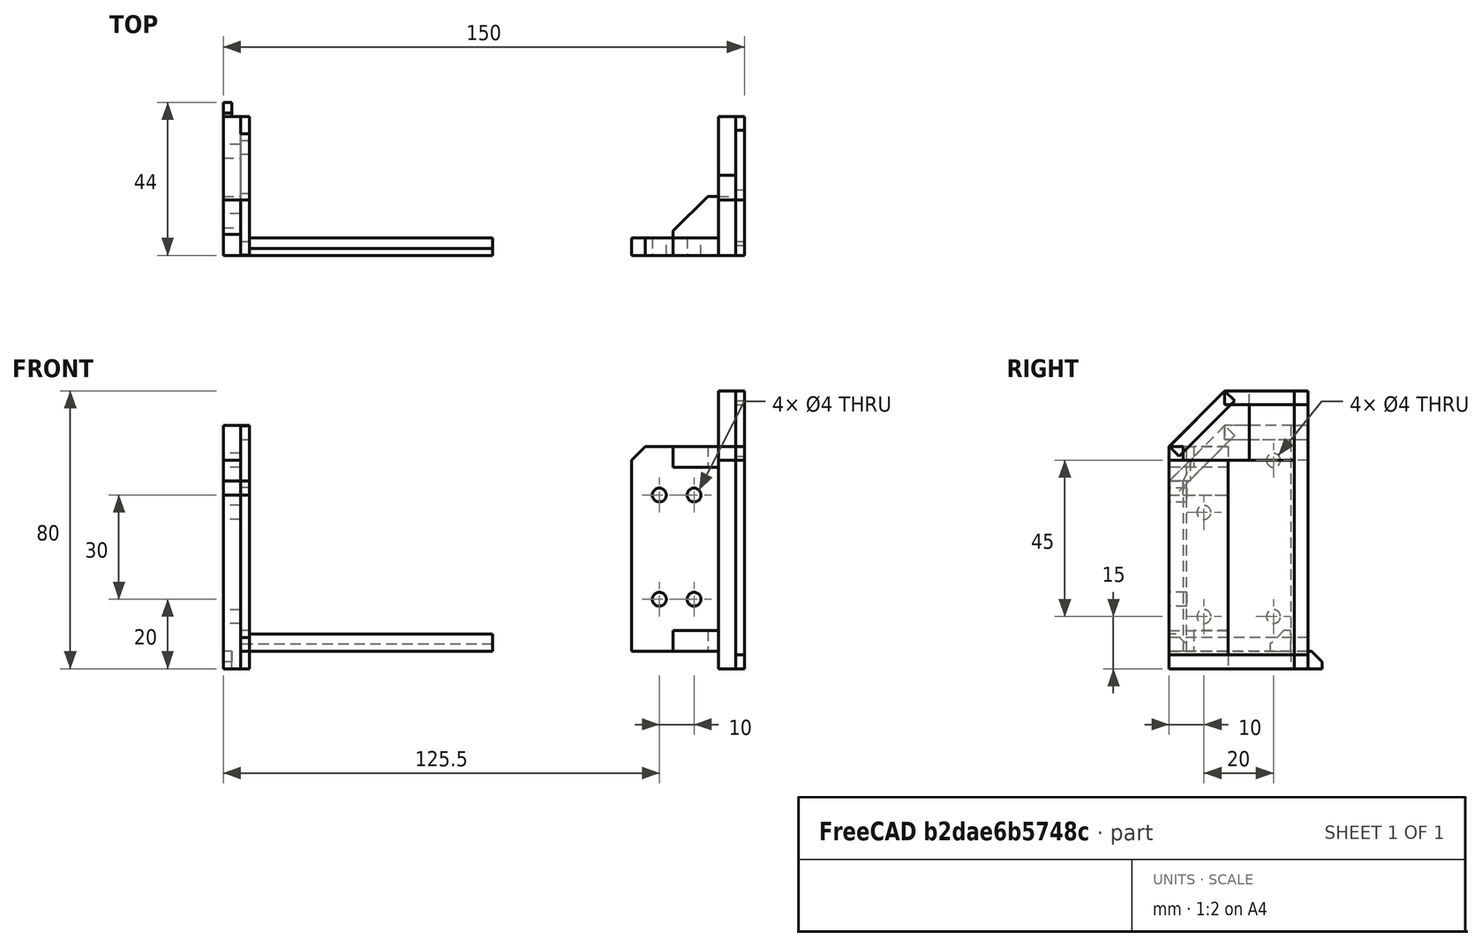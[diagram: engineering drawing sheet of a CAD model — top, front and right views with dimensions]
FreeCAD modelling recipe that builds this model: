
FCSTD DOCUMENT  (FreeCAD 0.20R29410 (Git))
Label: mount_02
License: All rights reserved
LicenseURL: http://en.wikipedia.org/wiki/All_rights_reserved
objects: Part::Extrusion×59, Part::Part2DObjectPython×41, Part::FeaturePython×20, Part::Cut×12, Part::Chamfer×11, Part::MultiFuse×4, Part::Fuse×1
note: 148 computed .brp shape members not serialized (recipe doc carries the construction recipe); baked Part::Feature solids carry a one-line shape summary decoded from their .brp

FEATURE [Part::Part2DObjectPython] Rectangle003  # Draft 2D object (typed FeaturePython)
  Area = 0
  ChamferSize = 0
  Columns = 1
  FilletRadius = 0
  Height = 60
  Length = 17
  MakeFace = false
  Placement = pos=(0,0,10) rot=(0.57735,0.57735,0.57735;2.0944rad)
  Rows = 1
FEATURE [Part::Part2DObjectPython] Rectangle011  # Draft 2D object (typed FeaturePython)
  Area = 0
  ChamferSize = 0
  Columns = 1
  FilletRadius = 0
  Height = 4
  Length = 24
  MakeFace = false
  Placement = pos=(5,16,86) rot=(0.57735,0.57735,0.57735;2.0944rad)
  Rows = 1
FEATURE [Part::Part2DObjectPython] Rectangle012  # Draft 2D object (typed FeaturePython)
  Area = 0
  ChamferSize = 0
  Columns = 1
  FilletRadius = 0
  Height = 4
  Length = 40
  MakeFace = false
  Placement = pos=(5,0,10) rot=(0.57735,0.57735,0.57735;2.0944rad)
  Rows = 1
FEATURE [Part::Extrusion] Extrude002
  Base = -> Rectangle003
  Dir = (1,0,0)
  DirMode = 2
  FaceMakerClass = Part::FaceMakerBullseye
  LengthFwd = 5
  LengthRev = 0
  Placement = pos=(-140,0,0) rot=(0,0,1;0rad)
  Solid = true
  Symmetric = false
FEATURE [Part::Part2DObjectPython] Rectangle  # Draft 2D object (typed FeaturePython)
  Area = 0
  ChamferSize = 0
  Columns = 1
  FilletRadius = 0
  Height = 60
  Length = 23
  MakeFace = false
  Placement = pos=(0,17,10) rot=(0.57735,0.57735,0.57735;2.0944rad)
  Rows = 1
FEATURE [Part::Part2DObjectPython] Rectangle013  # Draft 2D object (typed FeaturePython)
  Area = 0
  ChamferSize = 0
  Columns = 1
  FilletRadius = 0
  Height = 20
  Length = 17
  MakeFace = false
  Placement = pos=(0,0,70) rot=(0.57735,0.57735,0.57735;2.0944rad)
  Rows = 1
FEATURE [Part::Part2DObjectPython] Rectangle014  # Draft 2D object (typed FeaturePython)
  Area = 0
  ChamferSize = 0
  Columns = 1
  FilletRadius = 0
  Height = 20
  Length = 23
  MakeFace = false
  Placement = pos=(0,17,70) rot=(0.57735,0.57735,0.57735;2.0944rad)
  Rows = 1
FEATURE [Part::Extrusion] Extrude
  Base = -> Rectangle
  Dir = (1,-2e-16,2e-16)
  DirMode = 2
  FaceMakerClass = Part::FaceMakerBullseye
  LengthFwd = 5
  LengthRev = 0
  Solid = true
  Symmetric = false
FEATURE [Part::Extrusion] Extrude003
  Base = -> Rectangle014
  Dir = (1,-2e-16,2e-16)
  DirMode = 2
  FaceMakerClass = Part::FaceMakerBullseye
  LengthFwd = 5
  LengthRev = 0
  Placement = pos=(0,-17,0) rot=(0,0,1;0rad)
  Solid = true
  Symmetric = false
FEATURE [Part::Extrusion] Extrude004
  Base = -> Rectangle013
  Dir = (1,-2e-16,2e-16)
  DirMode = 2
  FaceMakerClass = Part::FaceMakerBullseye
  LengthFwd = 5
  LengthRev = 0
  Placement = pos=(0,23,0) rot=(0,0,1;0rad)
  Solid = true
  Symmetric = false
FEATURE [Part::Chamfer] Chamfer
  Base = -> Extrude003
  Edges = 1 edges r=16: [Edge8]
FEATURE [Part::Part2DObjectPython] Rectangle008  # Draft 2D object (typed FeaturePython)
  Area = 0
  ChamferSize = 0
  Columns = 1
  FilletRadius = 0
  Height = 4
  Length = 22.6
  MakeFace = false
  Placement = pos=(5,2.85,71.15) rot=(0.678598,0.281085,0.678598;2.59356rad)
  Rows = 1
FEATURE [Part::Part2DObjectPython] Rectangle015  # Draft 2D object (typed FeaturePython)
  Area = 0
  ChamferSize = 0
  Columns = 1
  FilletRadius = 0
  Height = 4
  Length = 4
  MakeFace = false
  Placement = pos=(5,0,70) rot=(0.57735,0.57735,0.57735;2.0944rad)
  Rows = 1
FEATURE [Part::Part2DObjectPython] Rectangle016  # Draft 2D object (typed FeaturePython)
  Area = 0
  ChamferSize = 0
  Columns = 1
  FilletRadius = 0
  Height = 80
  Length = 4
  MakeFace = false
  Placement = pos=(5,36,10) rot=(0.57735,0.57735,0.57735;2.0944rad)
  Rows = 1
FEATURE [Part::Extrusion] Extrude005
  Base = -> Rectangle008
  Dir = (1,-2.79271e-06,1.15679e-06)
  DirMode = 2
  FaceMakerClass = Part::FaceMakerBullseye
  LengthFwd = 2.5
  LengthRev = 0
  Solid = true
  Symmetric = false
FEATURE [Part::Extrusion] Extrude006
  Base = -> Rectangle015
  Dir = (1,-2e-16,2e-16)
  DirMode = 2
  FaceMakerClass = Part::FaceMakerBullseye
  LengthFwd = 2.5
  LengthRev = 0
  Solid = true
  Symmetric = false
FEATURE [Part::Extrusion] Extrude007
  Base = -> Rectangle011
  Dir = (1,-2e-16,2e-16)
  DirMode = 2
  FaceMakerClass = Part::FaceMakerBullseye
  LengthFwd = 2.5
  LengthRev = 0
  Solid = true
  Symmetric = false
FEATURE [Part::Extrusion] Extrude008
  Base = -> Rectangle016
  Dir = (1,-2e-16,2e-16)
  DirMode = 2
  FaceMakerClass = Part::FaceMakerBullseye
  LengthFwd = 2.5
  LengthRev = 0
  Solid = true
  Symmetric = false
FEATURE [Part::Extrusion] Extrude009
  Base = -> Rectangle012
  Dir = (1,-2e-16,2e-16)
  DirMode = 2
  FaceMakerClass = Part::FaceMakerBullseye
  LengthFwd = 2.5
  LengthRev = 0
  Solid = true
  Symmetric = false
FEATURE [Part::Part2DObjectPython] Rectangle017  # Draft 2D object (typed FeaturePython)
  Area = 0
  ChamferSize = 0
  Columns = 1
  FilletRadius = 0
  Height = 80
  Length = 5
  MakeFace = false
  Placement = pos=(0,35,10) rot=(0.57735,0.57735,0.57735;2.0944rad)
  Rows = 1
FEATURE [Part::Part2DObjectPython] Rectangle018  # Draft 2D object (typed FeaturePython)
  Area = 0
  ChamferSize = 0
  Columns = 1
  FilletRadius = 0
  Height = 5
  Length = 40
  MakeFace = false
  Placement = pos=(0,0,10) rot=(0.57735,0.57735,0.57735;2.0944rad)
  Rows = 1
FEATURE [Part::Part2DObjectPython] Rectangle019  # Draft 2D object (typed FeaturePython)
  Area = 0
  ChamferSize = 0
  Columns = 1
  FilletRadius = 0
  Height = 6
  Length = 6
  MakeFace = false
  Placement = pos=(0,29,15) rot=(0.57735,0.57735,0.57735;2.0944rad)
  Rows = 1
FEATURE [Part::Extrusion] Extrude010
  Base = -> Rectangle017
  Dir = (1,-2e-16,2e-16)
  DirMode = 2
  FaceMakerClass = Part::FaceMakerBullseye
  LengthFwd = -30
  LengthRev = 0
  Solid = true
  Symmetric = false
FEATURE [Part::Extrusion] Extrude011
  Base = -> Rectangle018
  Dir = (1,-2e-16,2e-16)
  DirMode = 2
  FaceMakerClass = Part::FaceMakerBullseye
  LengthFwd = -30
  LengthRev = 0
  Solid = true
  Symmetric = false
FEATURE [Part::Extrusion] Extrude012
  Base = -> Rectangle019
  Dir = (1,-2e-16,2e-16)
  DirMode = 2
  FaceMakerClass = Part::FaceMakerBullseye
  LengthFwd = -30
  LengthRev = 0
  Solid = true
  Symmetric = false
FEATURE [Part::Chamfer] Chamfer001
  Base = -> Extrude012
  Edges = 1 edges r=4: [Edge8]
FEATURE [Part::Part2DObjectPython] Rectangle020  # Draft 2D object (typed FeaturePython)
  Area = 0
  ChamferSize = 0
  Columns = 1
  FilletRadius = 0
  Height = 5
  Length = 4
  MakeFace = false
  Placement = pos=(7.5,40,85) rot=(0.57735,0.57735,0.57735;2.0944rad)
  Rows = 1
FEATURE [Part::Part2DObjectPython] Rectangle021  # Draft 2D object (typed FeaturePython)
  Area = 0
  ChamferSize = 0
  Columns = 1
  FilletRadius = 0
  Height = 5
  Length = 5
  MakeFace = false
  Placement = pos=(0,0,15) rot=(0.57735,0.57735,0.57735;2.0944rad)
  Rows = 1
FEATURE [Part::Part2DObjectPython] Rectangle022  # Draft 2D object (typed FeaturePython)
  Area = 0
  ChamferSize = 0
  Columns = 1
  FilletRadius = 0
  Height = 5
  Length = 5
  MakeFace = false
  Placement = pos=(0,30,85) rot=(0.57735,0.57735,0.57735;2.0944rad)
  Rows = 1
FEATURE [Part::Part2DObjectPython] Rectangle023  # Draft 2D object (typed FeaturePython)
  Area = 0
  ChamferSize = 0
  Columns = 1
  FilletRadius = 0
  Height = 5
  Length = 4
  MakeFace = false
  Placement = pos=(7.5,40,10) rot=(0.57735,0.57735,0.57735;2.0944rad)
  Rows = 1
FEATURE [Part::Extrusion] Extrude013
  Base = -> Rectangle020
  Dir = (1,-2e-16,2e-16)
  DirMode = 2
  FaceMakerClass = Part::FaceMakerBullseye
  LengthFwd = -37.5
  LengthRev = 0
  Solid = true
  Symmetric = false
FEATURE [Part::Extrusion] Extrude014
  Base = -> Rectangle023
  Dir = (1,-2e-16,2e-16)
  DirMode = 2
  FaceMakerClass = Part::FaceMakerBullseye
  LengthFwd = -37.5
  LengthRev = 0
  Solid = true
  Symmetric = false
FEATURE [Part::Extrusion] Extrude015
  Base = -> Rectangle022
  Dir = (1,0,0)
  DirMode = 2
  FaceMakerClass = Part::FaceMakerBullseye
  LengthFwd = -30
  LengthRev = 0
  Solid = true
  Symmetric = false
FEATURE [Part::Extrusion] Extrude016
  Base = -> Rectangle021
  Dir = (1,-2e-16,2e-16)
  DirMode = 2
  FaceMakerClass = Part::FaceMakerBullseye
  LengthFwd = -30
  LengthRev = 0
  Solid = true
  Symmetric = false
FEATURE [Part::Chamfer] Chamfer002
  Base = -> Extrude013
  Edges = 1 edges r=3: [Edge2]
FEATURE [Part::Chamfer] Chamfer003
  Base = -> Extrude014
  Edges = 1 edges r=3: [Edge5]
FEATURE [Part::Chamfer] Chamfer004
  Base = -> Extrude015
  Edges = 1 edges r=3: [Edge1]
FEATURE [Part::Chamfer] Chamfer005
  Base = -> Extrude016
  Edges = 1 edges r=3: [Edge5]
FEATURE [Part::Part2DObjectPython] Rectangle024  # Draft 2D object (typed FeaturePython)
  Area = 0
  ChamferSize = 0
  Columns = 1
  FilletRadius = 0
  Height = 60
  Length = 17
  MakeFace = false
  Placement = pos=(0,0,10) rot=(0.57735,0.57735,0.57735;2.0944rad)
  Rows = 1
FEATURE [Part::Extrusion] Extrude017
  Base = -> Rectangle024
  Dir = (1,0,0)
  DirMode = 2
  FaceMakerClass = Part::FaceMakerBullseye
  LengthFwd = 5
  LengthRev = 0
  Solid = true
  Symmetric = false
FEATURE [Part::Part2DObjectPython] Rectangle025  # Draft 2D object (typed FeaturePython)
  Area = 0
  ChamferSize = 0
  Columns = 1
  FilletRadius = 0
  Height = 60
  Length = 23
  MakeFace = false
  Placement = pos=(0,17,10) rot=(0.57735,0.57735,0.57735;2.0944rad)
  Rows = 1
FEATURE [Part::Extrusion] Extrude018
  Base = -> Rectangle025
  Dir = (1,-2e-16,2e-16)
  DirMode = 2
  FaceMakerClass = Part::FaceMakerBullseye
  LengthFwd = 5
  LengthRev = 0
  Placement = pos=(-140,0,0) rot=(0,0,1;0rad)
  Solid = true
  Symmetric = false
FEATURE [Part::Part2DObjectPython] Rectangle026  # Draft 2D object (typed FeaturePython)
  Area = 0
  ChamferSize = 0
  Columns = 1
  FilletRadius = 0
  Height = 20
  Length = 23
  MakeFace = false
  Placement = pos=(0,17,70) rot=(0.57735,0.57735,0.57735;2.0944rad)
  Rows = 1
FEATURE [Part::Extrusion] Extrude019
  Base = -> Rectangle026
  Dir = (1,-2e-16,2e-16)
  DirMode = 2
  FaceMakerClass = Part::FaceMakerBullseye
  LengthFwd = 5
  LengthRev = 0
  Placement = pos=(0,-17,0) rot=(0,0,1;0rad)
  Solid = true
  Symmetric = false
FEATURE [Part::Chamfer] Chamfer006
  Base = -> Extrude019
  Edges = 1 edges r=16: [Edge8]
  Placement = pos=(-140,0,0) rot=(0,0,1;0rad)
FEATURE [Part::Part2DObjectPython] Rectangle027  # Draft 2D object (typed FeaturePython)
  Area = 0
  ChamferSize = 0
  Columns = 1
  FilletRadius = 0
  Height = 20
  Length = 17
  MakeFace = false
  Placement = pos=(0,0,70) rot=(0.57735,0.57735,0.57735;2.0944rad)
  Rows = 1
FEATURE [Part::Extrusion] Extrude020
  Base = -> Rectangle027
  Dir = (1,-2e-16,2e-16)
  DirMode = 2
  FaceMakerClass = Part::FaceMakerBullseye
  LengthFwd = 5
  LengthRev = 0
  Placement = pos=(-140,23,0) rot=(0,0,1;0rad)
  Solid = true
  Symmetric = false
FEATURE [Part::FeaturePython] Facebinder  # WARN: FeaturePython — macro-defined, semantics opaque (R4)
  Area = 200
  Extrusion = 0
  Faces = -> [Extrude011]
  RemoveSplitter = false
  Sew = false
FEATURE [Part::Extrusion] Extrude021
  Base = -> Facebinder
  Dir = (-1,2e-16,-1e-16)
  DirMode = 2
  FaceMakerClass = Part::FaceMakerBullseye
  LengthFwd = 35
  LengthRev = 0
  Solid = false
  Symmetric = false
FEATURE [Part::FeaturePython] Facebinder001  # WARN: FeaturePython — macro-defined, semantics opaque (R4)
  Area = 400
  Extrusion = 0
  Faces = -> [Extrude010]
  RemoveSplitter = false
  Sew = false
FEATURE [Part::Extrusion] Extrude022
  Base = -> Facebinder001
  Dir = (-1,2e-16,-1e-16)
  DirMode = 2
  FaceMakerClass = Part::FaceMakerBullseye
  LengthFwd = 35
  LengthRev = 0
  Solid = false
  Symmetric = false
FEATURE [Part::FeaturePython] Facebinder002  # WARN: FeaturePython — macro-defined, semantics opaque (R4)
  Area = 28
  Extrusion = 0
  Faces = -> [Chamfer001]
  RemoveSplitter = false
  Sew = false
FEATURE [Part::Extrusion] Extrude023
  Base = -> Facebinder002
  Dir = (-1,2e-16,-1e-16)
  DirMode = 2
  FaceMakerClass = Part::FaceMakerBullseye
  LengthFwd = 35
  LengthRev = 0
  Solid = false
  Symmetric = false
FEATURE [Part::FeaturePython] Facebinder003  # WARN: FeaturePython — macro-defined, semantics opaque (R4)
  Area = 20.5
  Extrusion = 0
  Faces = -> [Chamfer005]
  RemoveSplitter = false
  Sew = false
FEATURE [Part::Extrusion] Extrude024
  Base = -> Facebinder003
  Dir = (-1,2e-16,-1e-16)
  DirMode = 2
  FaceMakerClass = Part::FaceMakerBullseye
  LengthFwd = 35
  LengthRev = 0
  Solid = false
  Symmetric = false
FEATURE [Part::FeaturePython] Facebinder004  # WARN: FeaturePython — macro-defined, semantics opaque (R4)
  Area = 20.5
  Extrusion = 0
  Faces = -> [Chamfer004]
  RemoveSplitter = false
  Sew = false
FEATURE [Part::Extrusion] Extrude025
  Base = -> Facebinder004
  Dir = (-1,0,0)
  DirMode = 2
  FaceMakerClass = Part::FaceMakerBullseye
  LengthFwd = 35
  LengthRev = 0
  Solid = false
  Symmetric = false
FEATURE [Part::FeaturePython] Facebinder005  # WARN: FeaturePython — macro-defined, semantics opaque (R4)
  Area = 15.5
  Extrusion = 0
  Faces = -> [Chamfer003]
  RemoveSplitter = false
  Sew = false
FEATURE [Part::FeaturePython] Facebinder006  # WARN: FeaturePython — macro-defined, semantics opaque (R4)
  Area = 15.5
  Extrusion = 0
  Faces = -> [Chamfer002]
  RemoveSplitter = false
  Sew = false
FEATURE [Part::Extrusion] Extrude026
  Base = -> Facebinder005
  Dir = (-1,2e-16,-2e-16)
  DirMode = 2
  FaceMakerClass = Part::FaceMakerBullseye
  LengthFwd = 40
  LengthRev = 0
  Solid = false
  Symmetric = false
FEATURE [Part::Extrusion] Extrude027
  Base = -> Facebinder006
  Dir = (-1,2e-16,-2e-16)
  DirMode = 2
  FaceMakerClass = Part::FaceMakerBullseye
  LengthFwd = 40
  LengthRev = 0
  Solid = false
  Symmetric = false
FEATURE [Part::FeaturePython] Facebinder007  # WARN: FeaturePython — macro-defined, semantics opaque (R4)
  Area = 620.5
  Extrusion = 0
  Faces = -> [Extrude022,Extrude021,Extrude025]
  RemoveSplitter = false
  Sew = false
FEATURE [Part::Extrusion] Extrude028
  Base = -> Facebinder007
  Dir = (-1,0,0)
  DirMode = 2
  FaceMakerClass = Part::FaceMakerBullseye
  LengthFwd = 70
  LengthRev = 0
  Solid = false
  Symmetric = false
FEATURE [Part::FeaturePython] Facebinder008  # WARN: FeaturePython — macro-defined, semantics opaque (R4)
  Area = 28
  Extrusion = 0
  Faces = -> [Extrude023]
  RemoveSplitter = false
  Sew = false
FEATURE [Part::FeaturePython] Facebinder009  # WARN: FeaturePython — macro-defined, semantics opaque (R4)
  Area = 20.5
  Extrusion = 0
  Faces = -> [Extrude024]
  RemoveSplitter = false
  Sew = false
FEATURE [Part::FeaturePython] Facebinder010  # WARN: FeaturePython — macro-defined, semantics opaque (R4)
  Area = 15.5
  Extrusion = 0
  Faces = -> [Extrude026]
  RemoveSplitter = false
  Sew = false
FEATURE [Part::FeaturePython] Facebinder011  # WARN: FeaturePython — macro-defined, semantics opaque (R4)
  Area = 15.5
  Extrusion = 0
  Faces = -> [Extrude027]
  RemoveSplitter = false
  Sew = false
FEATURE [Part::Extrusion] Extrude029
  Base = -> Facebinder011
  Dir = (-1,2e-16,-2e-16)
  DirMode = 2
  FaceMakerClass = Part::FaceMakerBullseye
  LengthFwd = 70
  LengthRev = 0
  Placement = pos=(5,0,0) rot=(0,0,1;0rad)
  Solid = false
  Symmetric = false
FEATURE [Part::Extrusion] Extrude030
  Base = -> Facebinder009
  Dir = (-1,2e-16,-1e-16)
  DirMode = 2
  FaceMakerClass = Part::FaceMakerBullseye
  LengthFwd = 70
  LengthRev = 0
  Solid = false
  Symmetric = false
FEATURE [Part::Extrusion] Extrude031
  Base = -> Facebinder010
  Dir = (-1,2e-16,-2e-16)
  DirMode = 2
  FaceMakerClass = Part::FaceMakerBullseye
  LengthFwd = 70
  LengthRev = 0
  Solid = false
  Symmetric = false
FEATURE [Part::Extrusion] Extrude032
  Base = -> Facebinder008
  Dir = (-1,2e-16,-1e-16)
  DirMode = 2
  FaceMakerClass = Part::FaceMakerBullseye
  LengthFwd = 70
  LengthRev = 0
  Solid = false
  Symmetric = false
FEATURE [Part::Part2DObjectPython] Rectangle028  # Draft 2D object (typed FeaturePython)
  Area = 0
  ChamferSize = 0
  Columns = 1
  FilletRadius = 0
  Height = 4
  Length = 22.6
  MakeFace = false
  Placement = pos=(5,2.85,71.15) rot=(0.678598,0.281085,0.678598;2.59356rad)
  Rows = 1
FEATURE [Part::Extrusion] Extrude033
  Base = -> Rectangle028
  Dir = (1,-2.79271e-06,1.15679e-06)
  DirMode = 2
  FaceMakerClass = Part::FaceMakerBullseye
  LengthFwd = 2.5
  LengthRev = 0
  Placement = pos=(-140,0,0) rot=(0,0,1;0rad)
  Solid = true
  Symmetric = false
FEATURE [Part::Part2DObjectPython] Rectangle029  # Draft 2D object (typed FeaturePython)
  Area = 0
  ChamferSize = 0
  Columns = 1
  FilletRadius = 0
  Height = 4
  Length = 24
  MakeFace = false
  Placement = pos=(5,16,86) rot=(0.57735,0.57735,0.57735;2.0944rad)
  Rows = 1
FEATURE [Part::Extrusion] Extrude034
  Base = -> Rectangle029
  Dir = (1,-2e-16,2e-16)
  DirMode = 2
  FaceMakerClass = Part::FaceMakerBullseye
  LengthFwd = 2.5
  LengthRev = 0
  Placement = pos=(-140,0,0) rot=(0,0,1;0rad)
  Solid = true
  Symmetric = false
FEATURE [Part::Part2DObjectPython] Rectangle030  # Draft 2D object (typed FeaturePython)
  Area = 0
  ChamferSize = 0
  Columns = 1
  FilletRadius = 0
  Height = 4
  Length = 4
  MakeFace = false
  Placement = pos=(5,0,70) rot=(0.57735,0.57735,0.57735;2.0944rad)
  Rows = 1
FEATURE [Part::Extrusion] Extrude035
  Base = -> Rectangle030
  Dir = (1,-2e-16,2e-16)
  DirMode = 2
  FaceMakerClass = Part::FaceMakerBullseye
  LengthFwd = 2.5
  LengthRev = 0
  Placement = pos=(-140,0,0) rot=(0,0,1;0rad)
  Solid = true
  Symmetric = false
FEATURE [Part::Part2DObjectPython] Rectangle031  # Draft 2D object (typed FeaturePython)
  Area = 0
  ChamferSize = 0
  Columns = 1
  FilletRadius = 0
  Height = 4
  Length = 40
  MakeFace = false
  Placement = pos=(5,0,10) rot=(0.57735,0.57735,0.57735;2.0944rad)
  Rows = 1
FEATURE [Part::Extrusion] Extrude036
  Base = -> Rectangle031
  Dir = (1,-2e-16,2e-16)
  DirMode = 2
  FaceMakerClass = Part::FaceMakerBullseye
  LengthFwd = 2.5
  LengthRev = 0
  Placement = pos=(-142.5,0,5) rot=(0,0,1;0rad)
  Solid = true
  Symmetric = false
FEATURE [Part::FeaturePython] Facebinder012  # WARN: FeaturePython — macro-defined, semantics opaque (R4)
  Area = 10
  Extrusion = 0
  Faces = -> [Extrude035]
  RemoveSplitter = false
  Sew = false
FEATURE [Part::Extrusion] Extrude037
  Base = -> Facebinder012
  Dir = (2e-16,-1e-16,-1)
  DirMode = 2
  FaceMakerClass = Part::FaceMakerBullseye
  LengthFwd = 55
  LengthRev = 0
  Solid = false
  Symmetric = false
FEATURE [Part::MultiFuse] Fusion
  Placement = pos=(0,0,-10) rot=(0,0,1;0rad)
  Shapes = -> [Chamfer006,Extrude020,Extrude033,Extrude034,Extrude035]
FEATURE [Part::Part2DObjectPython] Rectangle063  # Draft 2D object (typed FeaturePython)
  Area = 0
  ChamferSize = 0
  Columns = 1
  FilletRadius = 0
  Height = 6
  Length = 6
  MakeFace = false
  Placement = pos=(-250,6,64) rot=(0.57735,-0.57735,-0.57735;2.0944rad)
  Rows = 1
FEATURE [Part::Extrusion] Extrude077
  Base = -> Rectangle063
  Dir = (-1,-2e-16,2e-16)
  DirMode = 2
  FaceMakerClass = Part::FaceMakerBullseye
  LengthFwd = -7.5
  LengthRev = 0
  Placement = pos=(110,0,0) rot=(0,0,1;0rad)
  Solid = true
  Symmetric = false
FEATURE [Part::Part2DObjectPython] Rectangle064  # Draft 2D object (typed FeaturePython)
  Area = 0
  ChamferSize = 0
  Columns = 1
  FilletRadius = 0
  Height = 6
  Length = 6
  MakeFace = false
  Placement = pos=(-250,6,64) rot=(0.57735,-0.57735,-0.57735;2.0944rad)
  Rows = 1
FEATURE [Part::Extrusion] Extrude078
  Base = -> Rectangle064
  Dir = (-1,-2e-16,2e-16)
  DirMode = 2
  FaceMakerClass = Part::FaceMakerBullseye
  LengthFwd = -7.5
  LengthRev = 0
  Placement = pos=(110,0,0) rot=(0,0,1;0rad)
  Solid = true
  Symmetric = false
FEATURE [Part::Part2DObjectPython] Rectangle065  # Draft 2D object (typed FeaturePython)
  Area = 0
  ChamferSize = 0
  Columns = 1
  FilletRadius = 0
  Height = 6
  Length = 6
  MakeFace = false
  Placement = pos=(-250,6,64) rot=(0.57735,-0.57735,-0.57735;2.0944rad)
  Rows = 1
FEATURE [Part::Cut] Cut
  Base = -> Extrude002
  Tool = -> Extrude077
FEATURE [Part::Cut] Cut001
  Base = -> Extrude037
  Placement = pos=(-2.5,0,0) rot=(0,0,1;0rad)
  Tool = -> Extrude078
FEATURE [Part::Part2DObjectPython] Rectangle066  # Draft 2D object (typed FeaturePython)
  Area = 0
  ChamferSize = 0
  Columns = 1
  FilletRadius = 0
  Height = 10
  Length = 10
  MakeFace = false
  Placement = pos=(-125,30,90) rot=(0,0.707107,-0.707107;3.14159rad)
  Rows = 1
FEATURE [Part::Extrusion] Extrude079
  Base = -> Rectangle066
  Dir = (1e-16,-1,0)
  DirMode = 2
  FaceMakerClass = Part::FaceMakerBullseye
  LengthFwd = -14
  LengthRev = 0
  Solid = true
  Symmetric = false
FEATURE [Part::Part2DObjectPython] Rectangle067  # Draft 2D object (typed FeaturePython)
  Area = 0
  ChamferSize = 0
  Columns = 1
  FilletRadius = 0
  Height = 10
  Length = 10
  MakeFace = false
  Placement = pos=(-125,30,90) rot=(0,0.707107,-0.707107;3.14159rad)
  Rows = 1
FEATURE [Part::Extrusion] Extrude080
  Base = -> Rectangle067
  Dir = (1e-16,-1,0)
  DirMode = 2
  FaceMakerClass = Part::FaceMakerBullseye
  LengthFwd = -14
  LengthRev = 0
  Solid = true
  Symmetric = false
FEATURE [Part::MultiFuse] Fusion001
  Shapes = -> [Extrude028,Extrude029]
FEATURE [Part::Chamfer] Chamfer007
  Base = -> Extrude079
  Edges = 1 edges r=9: [Edge2]
FEATURE [Part::Cut] Cut002
  Base = -> Extrude080
  Placement = pos=(0,0,-1) rot=(0,0,1;0rad)
  Tool = -> Chamfer007
FEATURE [Part::FeaturePython] Facebinder013  # WARN: FeaturePython — macro-defined, semantics opaque (R4)
  Area = 126
  Extrusion = 0
  Faces = -> [Cut002]
  RemoveSplitter = false
  Sew = false
FEATURE [Part::Extrusion] Extrude081
  Base = -> Facebinder013
  Dir = (-1e-16,0,1)
  DirMode = 2
  FaceMakerClass = Part::FaceMakerBullseye
  LengthFwd = 1
  LengthRev = 0
  Solid = false
  Symmetric = false
FEATURE [Part::MultiFuse] Fusion002
  Placement = pos=(40,0,0) rot=(0,0,1;0rad)
  Shapes = -> [Cut002,Extrude081]
FEATURE [Part::FeaturePython] Facebinder014  # WARN: FeaturePython — macro-defined, semantics opaque (R4)
  Area = 140
  Extrusion = 0
  Faces = -> [Fusion002]
  RemoveSplitter = false
  Sew = false
FEATURE [Part::Extrusion] Extrude082
  Base = -> Facebinder014
  Dir = (-1,-1e-16,-1e-16)
  DirMode = 2
  FaceMakerClass = Part::FaceMakerBullseye
  LengthFwd = 40
  LengthRev = 0
  Solid = false
  Symmetric = false
FEATURE [Part::MultiFuse] Fusion003
  Shapes = -> [Fusion002,Extrude082]
FEATURE [Part::Cut] Cut003
  Base = -> Fusion001
  Tool = -> Fusion003
FEATURE [Part::Part2DObjectPython] Rectangle068  # Draft 2D object (typed FeaturePython)
  Area = 125
  ChamferSize = 0
  Columns = 1
  FilletRadius = 0
  Height = 5
  Length = 25
  MakeFace = true
  Placement = pos=(0,5,15) rot=(0,0,1;3.14159rad)
  Rows = 1
FEATURE [Part::Extrusion] Extrude083
  Base = -> Rectangle068
  Dir = (0,0,1)
  DirMode = 2
  FaceMakerClass = Part::FaceMakerBullseye
  LengthFwd = 59
  LengthRev = 0
  Solid = false
  Symmetric = false
FEATURE [Part::Chamfer] Chamfer008
  Base = -> Extrude083
  Edges = 1 edges r=4: [Edge7]
FEATURE [Part::Part2DObjectPython] Rectangle069  # Draft 2D object (typed FeaturePython)
  Area = 102
  ChamferSize = 0
  Columns = 1
  FilletRadius = 0
  Height = 6
  Length = 17
  MakeFace = true
  Placement = pos=(0,17,64) rot=(0.57735,-0.57735,-0.57735;2.0944rad)
  Rows = 1
FEATURE [Part::Extrusion] Extrude084
  Base = -> Rectangle069
  Dir = (-1,0,0)
  DirMode = 2
  FaceMakerClass = Part::FaceMakerBullseye
  LengthFwd = 13
  LengthRev = 0
  Solid = false
  Symmetric = false
FEATURE [Part::Chamfer] Chamfer009
  Base = -> Extrude084
  Edges = 1 edges r=10: [Edge12]
  Placement = pos=(0,0,4) rot=(0,0,1;0rad)
FEATURE [Part::Part2DObjectPython] Rectangle070  # Draft 2D object (typed FeaturePython)
  Area = 102
  ChamferSize = 0
  Columns = 1
  FilletRadius = 0
  Height = 6
  Length = 17
  MakeFace = true
  Placement = pos=(0,17,64) rot=(0.57735,-0.57735,-0.57735;2.0944rad)
  Rows = 1
FEATURE [Part::Extrusion] Extrude085
  Base = -> Rectangle070
  Dir = (-1,0,0)
  DirMode = 2
  FaceMakerClass = Part::FaceMakerBullseye
  LengthFwd = 13
  LengthRev = 0
  Solid = false
  Symmetric = false
FEATURE [Part::Chamfer] Chamfer010
  Base = -> Extrude085
  Edges = 1 edges r=10: [Edge12]
  Placement = pos=(0,0,-49) rot=(0,0,1;0rad)
FEATURE [Part::Part2DObjectPython] Rectangle071  # Draft 2D object (typed FeaturePython)
  Area = 140
  ChamferSize = 0
  Columns = 1
  FilletRadius = 0
  Height = 20
  Length = 7
  MakeFace = true
  Placement = pos=(-7,0,10) rot=(1,0,0;1.5708rad)
  Rows = 1
FEATURE [Part::Part2DObjectPython] Circle  # Draft 2D object (typed FeaturePython)
  Area = 12.5664
  FirstAngle = 0
  LastAngle = 0
  MakeFace = true
  Placement = pos=(-7,0,30) rot=(1,0,0;1.5708rad)
  Radius = 2
FEATURE [Part::Part2DObjectPython] Circle001  # Draft 2D object (typed FeaturePython)
  Area = 12.5664
  FirstAngle = 0
  LastAngle = 0
  MakeFace = true
  Placement = pos=(-17,0,60) rot=(1,0,0;1.5708rad)
  Radius = 2
FEATURE [Part::Part2DObjectPython] Circle002  # Draft 2D object (typed FeaturePython)
  Area = 12.5664
  FirstAngle = 0
  LastAngle = 0
  MakeFace = true
  Placement = pos=(-17,0,30) rot=(1,0,0;1.5708rad)
  Radius = 2
FEATURE [Part::Part2DObjectPython] Circle003  # Draft 2D object (typed FeaturePython)
  Area = 12.5664
  FirstAngle = 0
  LastAngle = 0
  MakeFace = true
  Placement = pos=(-7,0,60) rot=(1,0,0;1.5708rad)
  Radius = 2
FEATURE [Part::Extrusion] Extrude086
  Base = -> Circle003
  Dir = (0,-1,2e-16)
  DirMode = 2
  FaceMakerClass = Part::FaceMakerBullseye
  LengthFwd = -5
  LengthRev = 0
  Solid = false
  Symmetric = false
FEATURE [Part::Extrusion] Extrude087
  Base = -> Circle001
  Dir = (0,-1,2e-16)
  DirMode = 2
  FaceMakerClass = Part::FaceMakerBullseye
  LengthFwd = -5
  LengthRev = 0
  Solid = false
  Symmetric = false
FEATURE [Part::Extrusion] Extrude088
  Base = -> Circle002
  Dir = (0,-1,2e-16)
  DirMode = 2
  FaceMakerClass = Part::FaceMakerBullseye
  LengthFwd = -5
  LengthRev = 0
  Solid = false
  Symmetric = false
FEATURE [Part::Extrusion] Extrude089
  Base = -> Circle
  Dir = (0,-1,2e-16)
  DirMode = 2
  FaceMakerClass = Part::FaceMakerBullseye
  LengthFwd = -5
  LengthRev = 0
  Solid = false
  Symmetric = false
FEATURE [Part::Cut] Cut004
  Base = -> Chamfer008
  Tool = -> Extrude086
FEATURE [Part::Cut] Cut005
  Base = -> Cut004
  Tool = -> Extrude087
FEATURE [Part::Cut] Cut006
  Base = -> Cut005
  Tool = -> Extrude089
FEATURE [Part::Cut] Cut007
  Base = -> Cut006
  Tool = -> Extrude088
FEATURE [Part::Part2DObjectPython] Circle004  # Draft 2D object (typed FeaturePython)
  Area = 12.5664
  FirstAngle = 0
  LastAngle = 0
  MakeFace = true
  Placement = pos=(-140,10,55) rot=(0.57735,-0.57735,-0.57735;2.0944rad)
  Radius = 2
FEATURE [Part::Part2DObjectPython] Circle005  # Draft 2D object (typed FeaturePython)
  Area = 12.5664
  FirstAngle = 0
  LastAngle = 0
  MakeFace = true
  Placement = pos=(-140,30,25) rot=(0.57735,-0.57735,-0.57735;2.0944rad)
  Radius = 2
FEATURE [Part::Part2DObjectPython] Circle006  # Draft 2D object (typed FeaturePython)
  Area = 12.5664
  FirstAngle = 0
  LastAngle = 0
  MakeFace = true
  Placement = pos=(-140,10,25) rot=(0.57735,-0.57735,-0.57735;2.0944rad)
  Radius = 2
FEATURE [Part::Part2DObjectPython] Circle007  # Draft 2D object (typed FeaturePython)
  Area = 12.5664
  FirstAngle = 0
  LastAngle = 0
  MakeFace = true
  Placement = pos=(-140,30,70) rot=(0.57735,-0.57735,-0.57735;2.0944rad)
  Radius = 2
FEATURE [Part::Extrusion] Extrude090
  Base = -> Circle004
  Dir = (-1,-2e-16,2e-16)
  DirMode = 2
  FaceMakerClass = Part::FaceMakerBullseye
  LengthFwd = -5
  LengthRev = 0
  Solid = false
  Symmetric = false
FEATURE [Part::Extrusion] Extrude091
  Base = -> Circle006
  Dir = (-1,0,0)
  DirMode = 2
  FaceMakerClass = Part::FaceMakerBullseye
  LengthFwd = -5
  LengthRev = 0
  Solid = false
  Symmetric = false
FEATURE [Part::Extrusion] Extrude092
  Base = -> Circle005
  Dir = (-1,0,0)
  DirMode = 2
  FaceMakerClass = Part::FaceMakerBullseye
  LengthFwd = -5
  LengthRev = 0
  Solid = false
  Symmetric = false
FEATURE [Part::Extrusion] Extrude093
  Base = -> Circle007
  Dir = (-1,-2e-16,2e-16)
  DirMode = 2
  FaceMakerClass = Part::FaceMakerBullseye
  LengthFwd = -5
  LengthRev = 0
  Solid = false
  Symmetric = false
FEATURE [Part::Cut] Cut008
  Base = -> Cut
  Tool = -> Extrude091
FEATURE [Part::Cut] Cut009
  Base = -> Cut008
  Placement = pos=(-2.5,0,0) rot=(0,0,1;0rad)
  Tool = -> Extrude090
FEATURE [Part::Cut] Cut010
  Base = -> Extrude018
  Tool = -> Extrude092
FEATURE [Part::Fuse] Fusion004
  Base = -> Fusion
  Tool = -> Cut010
FEATURE [Part::Cut] Cut011
  Base = -> Fusion004
  Placement = pos=(-2.5,0,0) rot=(0,0,1;0rad)
  Tool = -> Extrude093
FEATURE [Part::FeaturePython] Facebinder015  # WARN: FeaturePython — macro-defined, semantics opaque (R4)
  Area = 175
  Extrusion = 0
  Faces = -> [Cut003]
  RemoveSplitter = false
  Sew = false
FEATURE [Part::Extrusion] Extrude094
  Base = -> Facebinder015
  Dir = (-1,2e-16,-1e-16)
  DirMode = 2
  FaceMakerClass = Part::FaceMakerBullseye
  LengthFwd = 2.5
  LengthRev = 0
  Solid = false
  Symmetric = false
FEATURE [Part::FeaturePython] Facebinder016  # WARN: FeaturePython — macro-defined, semantics opaque (R4)
  Area = 25
  Extrusion = 0
  Faces = -> [Cut003]
  RemoveSplitter = false
  Sew = false
FEATURE [Part::Extrusion] Extrude095
  Base = -> Facebinder016
  Dir = (-1,2e-16,-1e-16)
  DirMode = 2
  FaceMakerClass = Part::FaceMakerBullseye
  LengthFwd = 2.5
  LengthRev = 0
  Solid = false
  Symmetric = false
FEATURE [Part::FeaturePython] Facebinder017  # WARN: FeaturePython — macro-defined, semantics opaque (R4)
  Area = 325
  Extrusion = 0
  Faces = -> [Cut003]
  RemoveSplitter = false
  Sew = false
FEATURE [Part::Extrusion] Extrude096
  Base = -> Facebinder017
  Dir = (-1,2e-16,-1e-16)
  DirMode = 2
  FaceMakerClass = Part::FaceMakerBullseye
  LengthFwd = 2.5
  LengthRev = 0
  Solid = false
  Symmetric = false
FEATURE [Part::FeaturePython] Facebinder018  # WARN: FeaturePython — macro-defined, semantics opaque (R4)
  Area = 28
  Extrusion = 0
  Faces = -> [Extrude032]
  RemoveSplitter = false
  Sew = false
FEATURE [Part::Extrusion] Extrude097
  Base = -> Facebinder018
  Dir = (-1,2e-16,-1e-16)
  DirMode = 2
  FaceMakerClass = Part::FaceMakerBullseye
  LengthFwd = 2.5
  LengthRev = 0
  Solid = false
  Symmetric = false
FEATURE [Part::FeaturePython] Facebinder019  # WARN: FeaturePython — macro-defined, semantics opaque (R4)
  Area = 15.5
  Extrusion = 0
  Faces = -> [Extrude031]
  RemoveSplitter = false
  Sew = false
FEATURE [Part::Extrusion] Extrude098
  Base = -> Facebinder019
  Dir = (-1,2e-16,-2e-16)
  DirMode = 2
  FaceMakerClass = Part::FaceMakerBullseye
  LengthFwd = 2.5
  LengthRev = 0
  Solid = false
  Symmetric = false
